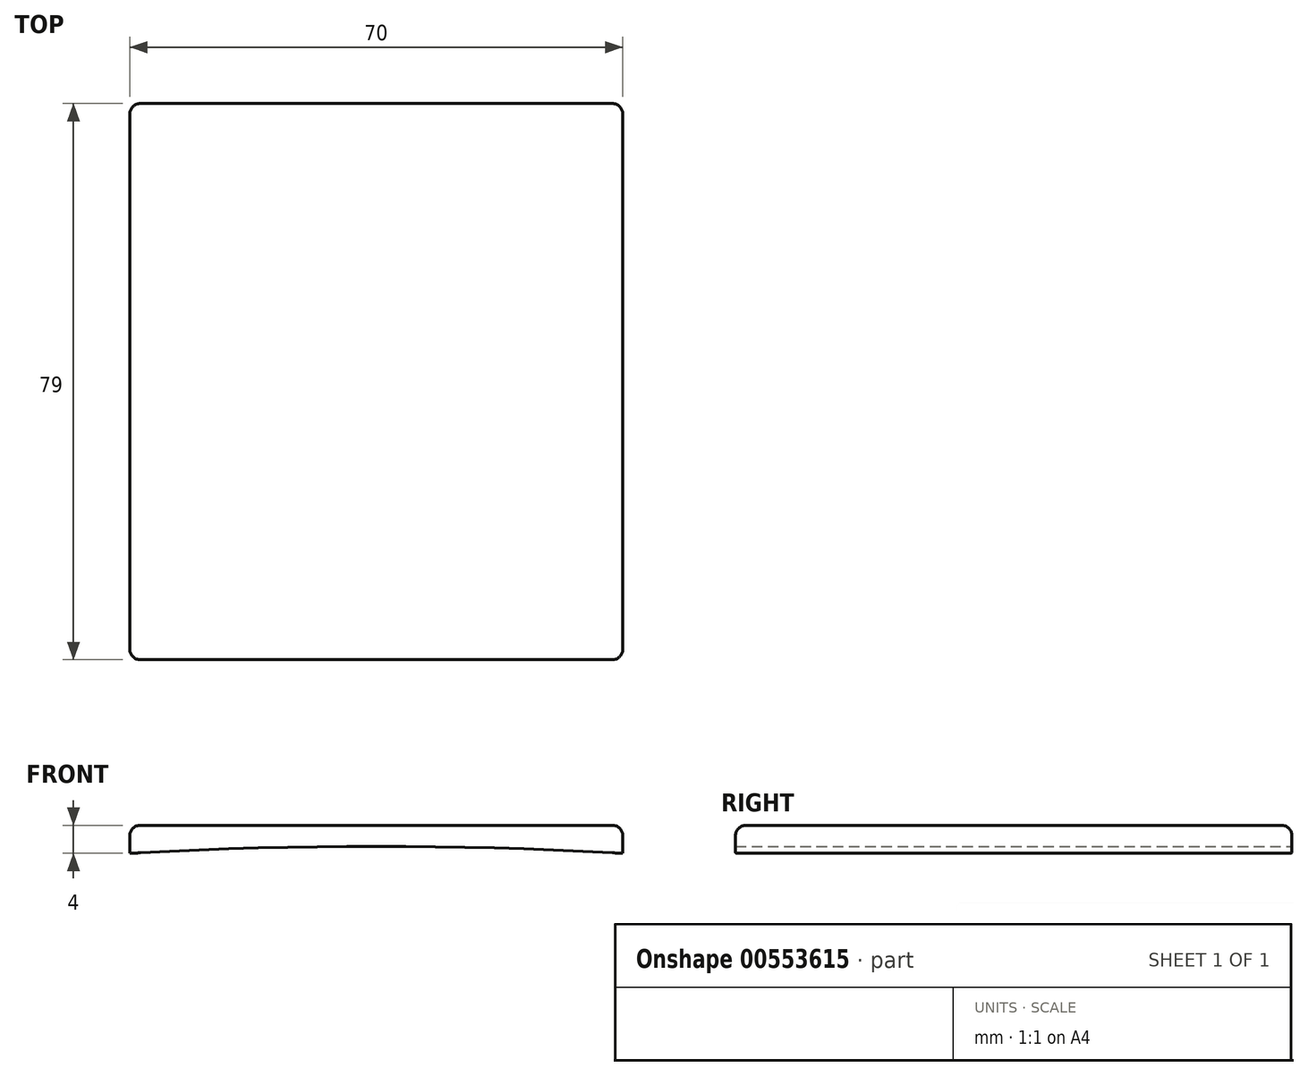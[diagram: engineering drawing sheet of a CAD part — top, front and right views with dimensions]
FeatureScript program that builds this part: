
annotation { "Feature Type Name" : "Feature", "Feature Type Description" : "" }
export const myFeature = defineFeature(function(context is Context, id is Id, definition is map)
    precondition{}
    {
        {
            var Q0;
            Q0=qCreatedBy(makeId("Front.planeOp"),FACE);
            var sketch = newSketch(context, id + "F0", { "sketchPlane" : qUnion([Q0])});
            skLineSegment(sketch, "E0", {"start": v(-33.5, 3) * mm, "end": v(33.5, 3) * mm});
            skLineSegment(sketch, "E1", {"start": v(-35, 1.5) * mm, "end": v(-35, -1) * mm});
            skLineSegment(sketch, "E2", {"start": v(35, 1.5) * mm, "end": v(35, -1) * mm});
            skArc(sketch, "E3", {"start": v(35, -1) * mm, "mid": v(0, 0) * mm, "end": v(-35, -1) * mm});
            skPoint(sketch, "E4.visualSharp", {"position": v(35, 3) * mm});
            skArc(sketch, "E4.filletArc", {"start": v(35, 1.5) * mm, "mid": v(34.56, 2.56) * mm, "end": v(33.5, 3) * mm});
            skPoint(sketch, "E5.visualSharp", {"position": v(-35, 3) * mm});
            skArc(sketch, "E5.filletArc", {"start": v(-33.5, 3) * mm, "mid": v(-34.56, 2.56) * mm, "end": v(-35, 1.5) * mm});
            skSolve(sketch);
        }
        {
            var Q0;
            Q0=makeQuery(id+"F0.imprint","IMPRINT",FACE,{"disambiguationData":[TD([[makeQuery(id+"F0.imprint","IMPRINT",EDGE,{"derivedFrom":sQuery(id+"F0.wireOp",EDGE,"E0")}),-1.0]])]});
            extrude(context, id + "F1", {"entities" : qUnion([Q0]), "depth" : 79 * mm});
        }
        {
            var Q0;
            Q0=makeQuery(id+"F1.opExtrude","SWEPT_EDGE",EDGE,{"disambiguationData":[OSD([sQuery(id+"F0.wireOp",EDGE,"E0"),sQuery(id+"F0.wireOp",EDGE,"E4.filletArc")])]});
            var Q1;
            Q1=makeQuery(id+"F1.opExtrude","SWEPT_FACE",FACE,{"disambiguationData":[OSD([sQuery(id+"F0.wireOp",EDGE,"E4.filletArc")])]});
            fillet(context, id + "F2", {"entities" : qUnion([Q0, Q1]), "radius" : 1.5 * mm, "tangentPropagation" : true, "allowEdgeOverflow" : false});
        }
    });
